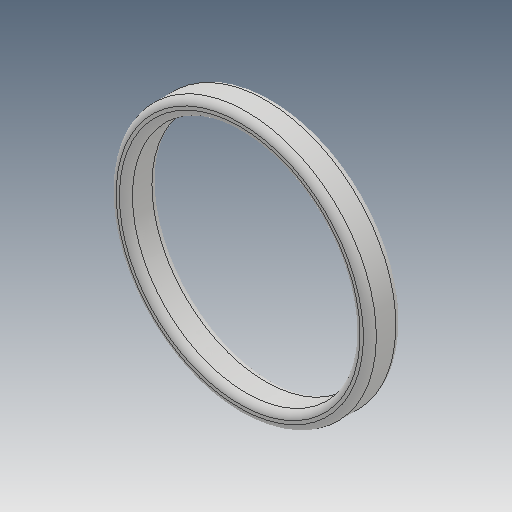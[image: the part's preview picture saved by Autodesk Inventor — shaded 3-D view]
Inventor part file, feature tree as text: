
AUTODESK INVENTOR PART (.ipt)
format: ipt  version: 2018 (Build 220112000, 112)  size: 144,896 bytes
history: native  units: mm
features: fillet x1
ambient origin geometry x8: Origin, YZ Plane, XZ Plane, XY Plane, X Axis, Y Axis, Z Axis, Center Point
bodies: Volumenkörper1 (feature_tree)
feature tree (1):
  fillet  "Fillet1"  [1 undecoded]
note: 1 required parameter value undecoded (feature->parameter linkage not recoverable at this tier; creation-order binding heuristic only, values carry confidence <= 0.55)
